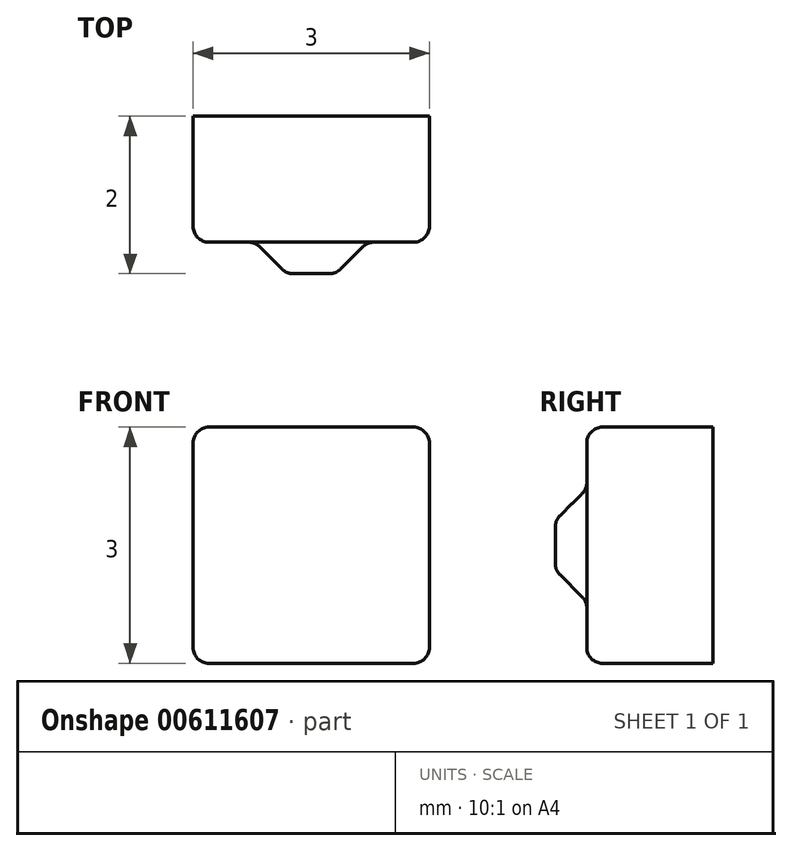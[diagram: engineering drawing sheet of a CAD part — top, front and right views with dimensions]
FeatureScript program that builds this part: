
annotation { "Feature Type Name" : "Feature", "Feature Type Description" : "" }
export const myFeature = defineFeature(function(context is Context, id is Id, definition is map)
    precondition{}
    {
        {
            var Q0;
            Q0=qCreatedBy(makeId("Front.planeOp"),FACE);
            var sketch = newSketch(context, id + "F0", { "sketchPlane" : qUnion([Q0])});
            skLineSegment(sketch, "E0.bottom", {"start": v(2.54, 5.54) * mm, "end": v(5.54, 5.54) * mm});
            skLineSegment(sketch, "E0.top", {"start": v(2.54, 2.54) * mm, "end": v(5.54, 2.54) * mm});
            skLineSegment(sketch, "E0.left", {"start": v(2.54, 5.54) * mm, "end": v(2.54, 2.54) * mm});
            skLineSegment(sketch, "E0.right", {"start": v(5.54, 5.54) * mm, "end": v(5.54, 2.54) * mm});
            skSolve(sketch);
        }
        {
            var Q0;
            Q0 = qSketchRegion(id + "F0", true);
            extrude(context, id + "F1", {"entities" : qUnion([Q0]), "depth" : 1.6 * mm, "offsetDistance" : 25 * mm});
        }
        {
            var Q0;
            Q0=makeQuery(id+"F1.opExtrude","CAP_FACE",FACE,{"disambiguationData":[OSD([sQuery(id+"F0.wireOp",EDGE,"E0.bottom"),sQuery(id+"F0.wireOp",EDGE,"E0.top"),sQuery(id+"F0.wireOp",EDGE,"E0.left"),sQuery(id+"F0.wireOp",EDGE,"E0.right")])],"isStart":false});
            var sketch = newSketch(context, id + "F2", { "sketchPlane" : qUnion([Q0])});
            skCircle(sketch, "E1", {"center": v(4.04, 4.04) * mm, "radius": 0.72 * mm});
            skSolve(sketch);
        }
        {
            var Q0;
            Q0 = qSketchRegion(id + "F2", true);
            extrude(context, id + "F3", {"entities" : qUnion([Q0]), "operationType" : NewBodyOperationType.ADD, "depth" : .4 * mm, "offsetDistance" : 25 * mm});
        }
        {
            var Q0;
            Q0=makeQuery(id+"F3.opExtrude","CAP_EDGE",EDGE,{"disambiguationData":[OSD([sQuery(id+"F2.wireOp",EDGE,"E1")])],"isStart":false});
            chamfer(context, id + "F4", {"entities" : qUnion([Q0]), "width" : .4 * mm, "tangentPropagation" : true});
        }
        {
            var Q0;
            {var subQ0=sQuery(id+"F2.wireOp",EDGE,"E1");Q0=makeQuery(id+"F4.opChamfer","BLEND_EDGE",EDGE,{"blendedFrom":[makeQuery(id+"F3.opExtrude","CAP_EDGE",EDGE,{"disambiguationData":[OSD([subQ0])],"isStart":false}),makeQuery(id+"F3.opExtrude","CAP_FACE",FACE,{"disambiguationData":[OSD([subQ0])],"isStart":false})],"blendedInto":[makeQuery(id+"F3.opExtrude","CAP_FACE",FACE,{"disambiguationData":[OSD([subQ0])],"isStart":false})]});}
            var Q1;
            Q1=makeQuery(id+"F4.opChamfer","BLEND_EDGE",EDGE,{"blendedFrom":[makeQuery(id+"F3.opExtrude","CAP_EDGE",EDGE,{"disambiguationData":[OSD([sQuery(id+"F2.wireOp",EDGE,"E1")])],"isStart":false}),makeQuery(id+"F1.opExtrude","CAP_FACE",FACE,{"disambiguationData":[OSD([sQuery(id+"F0.wireOp",EDGE,"E0.bottom"),sQuery(id+"F0.wireOp",EDGE,"E0.top"),sQuery(id+"F0.wireOp",EDGE,"E0.left"),sQuery(id+"F0.wireOp",EDGE,"E0.right")])],"isStart":false})],"blendedInto":[makeQuery(id+"F1.opExtrude","CAP_FACE",FACE,{"disambiguationData":[OSD([sQuery(id+"F0.wireOp",EDGE,"E0.bottom"),sQuery(id+"F0.wireOp",EDGE,"E0.top"),sQuery(id+"F0.wireOp",EDGE,"E0.left"),sQuery(id+"F0.wireOp",EDGE,"E0.right")])],"isStart":false})]});
            fillet(context, id + "F5", {"entities" : qUnion([Q0, Q1]), "radius" : .2 * mm, "tangentPropagation" : true, "allowEdgeOverflow" : false});
        }
        {
            var Q0;
            Q0=makeQuery(id+"F1.opExtrude","CAP_EDGE",EDGE,{"disambiguationData":[OSD([sQuery(id+"F0.wireOp",EDGE,"E0.left")])],"isStart":false});
            var Q1;
            Q1=makeQuery(id+"F1.opExtrude","CAP_EDGE",EDGE,{"disambiguationData":[OSD([sQuery(id+"F0.wireOp",EDGE,"E0.top")])],"isStart":false});
            var Q2;
            Q2=makeQuery(id+"F1.opExtrude","CAP_EDGE",EDGE,{"disambiguationData":[OSD([sQuery(id+"F0.wireOp",EDGE,"E0.right")])],"isStart":false});
            var Q3;
            Q3=makeQuery(id+"F1.opExtrude","CAP_EDGE",EDGE,{"disambiguationData":[OSD([sQuery(id+"F0.wireOp",EDGE,"E0.bottom")])],"isStart":false});
            var Q4;
            Q4=makeQuery(id+"F1.opExtrude","SWEPT_EDGE",EDGE,{"disambiguationData":[OSD([sQuery(id+"F0.wireOp",EDGE,"E0.top"),sQuery(id+"F0.wireOp",EDGE,"E0.right")])]});
            var Q5;
            Q5=makeQuery(id+"F1.opExtrude","SWEPT_EDGE",EDGE,{"disambiguationData":[OSD([sQuery(id+"F0.wireOp",EDGE,"E0.bottom"),sQuery(id+"F0.wireOp",EDGE,"E0.right")])]});
            var Q6;
            Q6=makeQuery(id+"F1.opExtrude","SWEPT_EDGE",EDGE,{"disambiguationData":[OSD([sQuery(id+"F0.wireOp",EDGE,"E0.top"),sQuery(id+"F0.wireOp",EDGE,"E0.left")])]});
            var Q7;
            Q7=makeQuery(id+"F1.opExtrude","SWEPT_EDGE",EDGE,{"disambiguationData":[OSD([sQuery(id+"F0.wireOp",EDGE,"E0.bottom"),sQuery(id+"F0.wireOp",EDGE,"E0.left")])]});
            fillet(context, id + "F6", {"entities" : qUnion([Q0, Q1, Q2, Q3, Q4, Q5, Q6, Q7]), "radius" : .2 * mm, "tangentPropagation" : true, "allowEdgeOverflow" : false});
        }
    });
